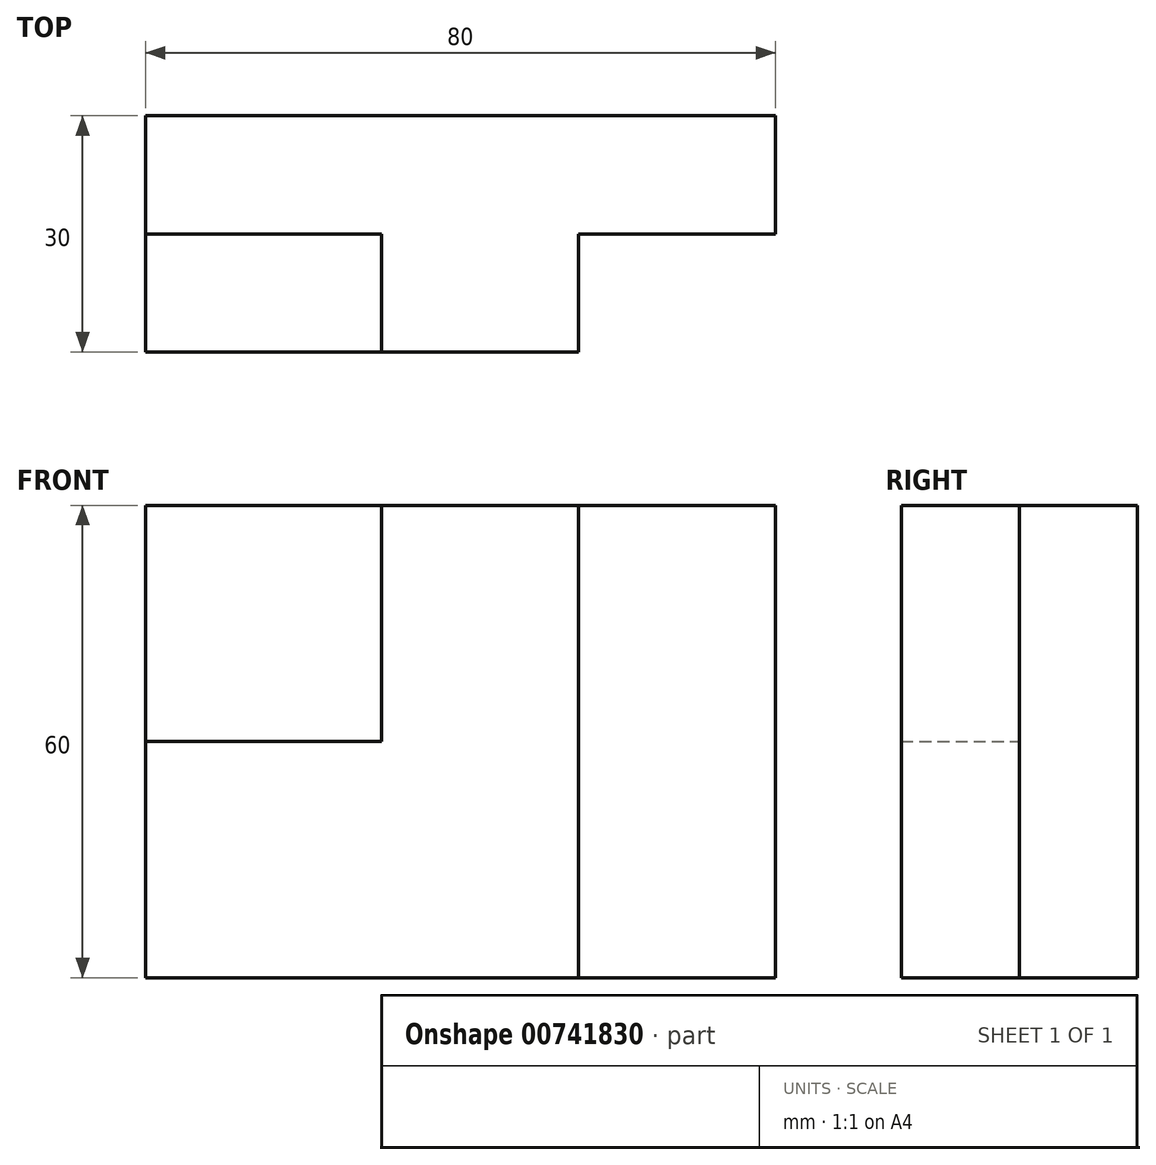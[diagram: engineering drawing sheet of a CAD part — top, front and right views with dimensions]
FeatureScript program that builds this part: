
annotation { "Feature Type Name" : "Feature", "Feature Type Description" : "" }
export const myFeature = defineFeature(function(context is Context, id is Id, definition is map)
    precondition{}
    {
        {
            var Q0;
            Q0=qCreatedBy(makeId("Front.planeOp"),FACE);
            var sketch = newSketch(context, id + "F0", { "sketchPlane" : qUnion([Q0])});
            skLineSegment(sketch, "E0.bottom", {"start": v(0, 0) * mm, "end": v(80, 0) * mm});
            skLineSegment(sketch, "E0.top", {"start": v(0, 60) * mm, "end": v(80, 60) * mm});
            skLineSegment(sketch, "E0.left", {"start": v(0, 0) * mm, "end": v(0, 60) * mm});
            skLineSegment(sketch, "E0.right", {"start": v(80, 0) * mm, "end": v(80, 60) * mm});
            skLineSegment(sketch, "E1.bottom", {"start": v(55, 60) * mm, "end": v(80, 60) * mm});
            skLineSegment(sketch, "E1.top", {"start": v(55, 0) * mm, "end": v(80, 0) * mm});
            skLineSegment(sketch, "E1.left", {"start": v(55, 60) * mm, "end": v(55, 0) * mm});
            skLineSegment(sketch, "E1.right", {"start": v(80, 60) * mm, "end": v(80, 0) * mm});
            skLineSegment(sketch, "E2.bottom", {"start": v(30, 60) * mm, "end": v(0, 60) * mm});
            skLineSegment(sketch, "E2.top", {"start": v(30, 30) * mm, "end": v(0, 30) * mm});
            skLineSegment(sketch, "E2.left", {"start": v(30, 60) * mm, "end": v(30, 30) * mm});
            skLineSegment(sketch, "E2.right", {"start": v(0, 60) * mm, "end": v(0, 30) * mm});
            skSolve(sketch);
        }
        {
            var Q0;
            {var subQ0=sQuery(id+"F0.wireOp",EDGE,"E1.left");Q0=makeQuery(id+"F0.imprint","IMPRINT",FACE,{"disambiguationData":[TD([[makeQuery(id+"F0.imprint","IMPRINT",EDGE,{"derivedFrom":subQ0}),-1.0]])]});}
            extrude(context, id + "F1", {"entities" : qUnion([Q0]), "depth" : 30 * mm, "offsetDistance" : 25 * mm});
        }
        {
            var Q0;
            {var subQ4=sQuery(id+"F0.wireOp",EDGE,"E2.top");Q0=makeQuery(id+"F0.imprint","IMPRINT",FACE,{"disambiguationData":[TD([[makeQuery(id+"F0.imprint","IMPRINT",EDGE,{"derivedFrom":subQ4}),-1.0]])]});}
            var Q1;
            {var subQ0=sQuery(id+"F0.wireOp",EDGE,"E0.right");Q1=makeQuery(id+"F0.imprint","IMPRINT",FACE,{"disambiguationData":[TD([[makeQuery(id+"F0.imprint","IMPRINT",EDGE,{"derivedFrom":subQ0}),1.0]])]});}
            extrude(context, id + "F2", {"entities" : qUnion([Q0, Q1]), "operationType" : NewBodyOperationType.ADD, "depth" : 15 * mm, "offsetDistance" : 25 * mm});
        }
    });
